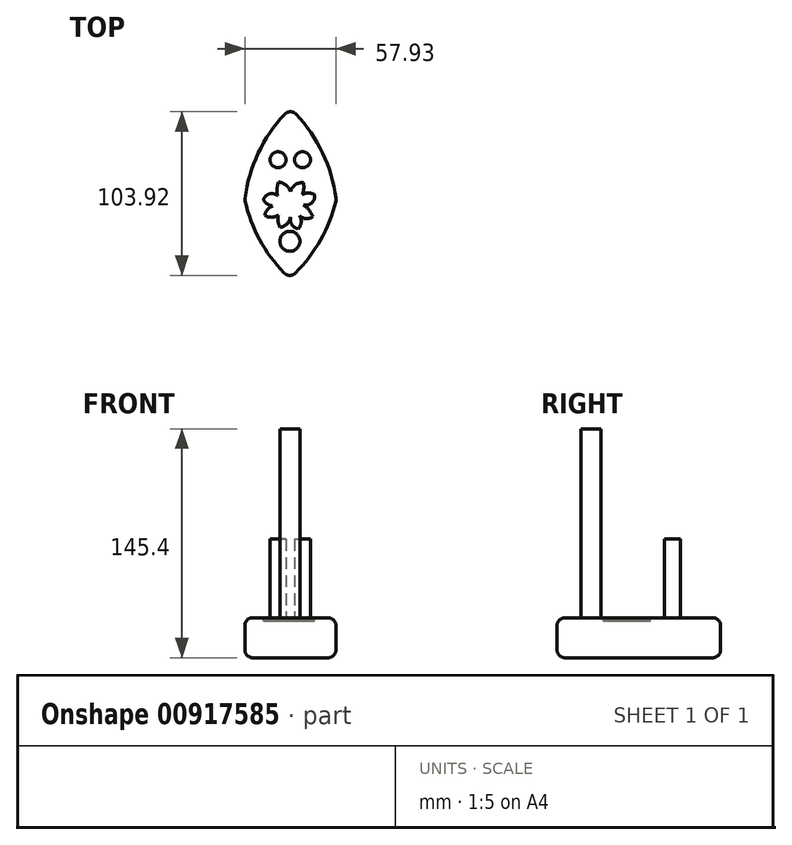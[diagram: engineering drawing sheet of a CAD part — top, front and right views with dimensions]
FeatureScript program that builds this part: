
annotation { "Feature Type Name" : "Feature", "Feature Type Description" : "" }
export const myFeature = defineFeature(function(context is Context, id is Id, definition is map)
    precondition{}
    {
        {
            var Q0;
            Q0=qCreatedBy(makeId("Top.planeOp"),FACE);
            var sketch = newSketch(context, id + "F0", { "sketchPlane" : qUnion([Q0])});
            skArc(sketch, "E0", {"start": v(0, 58.02) * mm, "mid": v(-19.52, 31.51) * mm, "end": v(-29.04, 0) * mm});
            skArc(sketch, "E1", {"start": v(-29.04, 0) * mm, "mid": v(-18.4, -27.48) * mm, "end": v(0, -50.5) * mm});
            skArc(sketch, "E2", {"start": v(-1.4, -50.82) * mm, "mid": v(17.8, -27.8) * mm, "end": v(29.04, 0) * mm});
            skArc(sketch, "E3", {"start": v(29.04, 0) * mm, "mid": v(19.52, 31.51) * mm, "end": v(0, 58.02) * mm});
            skSolve(sketch);
        }
        {
            var Q0;
            Q0 = qSketchRegion(id + "F0", true);
            extrude(context, id + "F1", {"entities" : qUnion([Q0]), "depth" : 25.4 * mm, "offsetDistance" : 25.4 * mm});
        }
        {
            var Q0;
            Q0=makeQuery(id+"F1.opExtrude","SWEPT_FACE",FACE,{"disambiguationData":[OSD([sQuery(id+"F0.wireOp",EDGE,"E1")])]});
            var Q1;
            Q1=makeQuery(id+"F1.opExtrude","SWEPT_FACE",FACE,{"disambiguationData":[OSD([sQuery(id+"F0.wireOp",EDGE,"E2")])]});
            var Q2;
            Q2=makeQuery(id+"F1.opExtrude","CAP_EDGE",EDGE,{"disambiguationData":[OSD([sQuery(id+"F0.wireOp",EDGE,"E3")])],"isStart":false});
            var Q3;
            Q3=makeQuery(id+"F1.opExtrude","CAP_EDGE",EDGE,{"disambiguationData":[OSD([sQuery(id+"F0.wireOp",EDGE,"E0")])],"isStart":false});
            var Q4;
            Q4=makeQuery(id+"F1.opExtrude","SWEPT_FACE",FACE,{"disambiguationData":[OSD([sQuery(id+"F0.wireOp",EDGE,"E0")])]});
            var Q5;
            Q5=makeQuery(id+"F1.opExtrude","SWEPT_FACE",FACE,{"disambiguationData":[OSD([sQuery(id+"F0.wireOp",EDGE,"E3")])]});
            var Q6;
            Q6=makeQuery(id+"F1.opExtrude","CAP_FACE",FACE,{"disambiguationData":[OSD([sQuery(id+"F0.wireOp",EDGE,"E0"),sQuery(id+"F0.wireOp",EDGE,"E1"),sQuery(id+"F0.wireOp",EDGE,"E2"),sQuery(id+"F0.wireOp",EDGE,"E3")])],"isStart":false});
            fillet(context, id + "F2", {"entities" : qUnion([Q0, Q1, Q2, Q3, Q4, Q5, Q6]), "radius" : 5.08 * mm, "tangentPropagation" : true, "allowEdgeOverflow" : false});
        }
        {
            var Q0;
            Q0=makeQuery(id+"F1.opExtrude","CAP_FACE",FACE,{"disambiguationData":[OSD([sQuery(id+"F0.wireOp",EDGE,"E0"),sQuery(id+"F0.wireOp",EDGE,"E1"),sQuery(id+"F0.wireOp",EDGE,"E2"),sQuery(id+"F0.wireOp",EDGE,"E3")])],"isStart":false});
            var sketch = newSketch(context, id + "F3", { "sketchPlane" : qUnion([Q0])});
            skLineSegment(sketch, "E4", {"start": v(-23.89, 0.24) * mm, "end": v(23.88, 0.27) * mm});
            skLineSegment(sketch, "E5", {"start": v(0, 50.79) * mm, "end": v(-0.45, -42.97) * mm});
            skCircle(sketch, "E6", {"center": v(-0.37, -26.4) * mm, "radius": 6.35 * mm});
            skCircle(sketch, "E7", {"center": v(-7.94, 25.39) * mm, "radius": 5.08 * mm});
            skCircle(sketch, "E8", {"center": v(7.7, 25.39) * mm, "radius": 5.08 * mm});
            skSolve(sketch);
        }
        {
            var Q0;
            {var subQ0=sQuery(id+"F3.wireOp",EDGE,"E6");var subQ1=sQuery(id+"F3.wireOp",EDGE,"E5");var subQ2=makeQuery(id+"F3.imprint","INTERSECT",VERTEX,{"disambiguationData":[OD(0.0)],"derivedFrom":[subQ1,subQ0]});Q0=makeQuery(id+"F3.imprint","IMPRINT",FACE,{"disambiguationData":[TD([[makeQuery(id+"F3.imprint","IMPRINT",EDGE,{"disambiguationData":[TD([[subQ2,-1.0]])],"derivedFrom":subQ1}),1.0]])]});}
            var Q1;
            {var subQ0=sQuery(id+"F3.wireOp",EDGE,"E6");var subQ1=sQuery(id+"F3.wireOp",EDGE,"E5");var subQ2=makeQuery(id+"F3.imprint","INTERSECT",VERTEX,{"disambiguationData":[OD(0.0)],"derivedFrom":[subQ1,subQ0]});Q1=makeQuery(id+"F3.imprint","IMPRINT",FACE,{"disambiguationData":[TD([[makeQuery(id+"F3.imprint","IMPRINT",EDGE,{"disambiguationData":[TD([[subQ2,-1.0]])],"derivedFrom":subQ1}),-1.0]])]});}
            extrude(context, id + "F4", {"entities" : qUnion([Q0, Q1]), "operationType" : NewBodyOperationType.ADD, "depth" : 120 * mm, "offsetDistance" : 25.4 * mm});
        }
        {
            var Q0;
            Q0=makeQuery(id+"F3.imprint","IMPRINT",FACE,{"disambiguationData":[TD([[makeQuery(id+"F3.imprint","IMPRINT",EDGE,{"derivedFrom":sQuery(id+"F3.wireOp",EDGE,"E8")}),1.0]])]});
            var Q1;
            Q1=makeQuery(id+"F3.imprint","IMPRINT",FACE,{"disambiguationData":[TD([[makeQuery(id+"F3.imprint","IMPRINT",EDGE,{"derivedFrom":sQuery(id+"F3.wireOp",EDGE,"E7")}),1.0]])]});
            var Q2;
            Q2=sQuery(id+"F3.wireOp",EDGE,"E7");
            var Q3;
            Q3=sQuery(id+"F3.wireOp",EDGE,"E8");
            extrude(context, id + "F5", {"entities" : qUnion([Q0, Q1]), "surfaceEntities" : qUnion([Q2, Q3]), "depth" : 50 * mm, "offsetDistance" : 25 * mm});
        }
        {
            var Q0;
            Q0=makeQuery(id+"F1.opExtrude","CAP_FACE",FACE,{"disambiguationData":[OSD([sQuery(id+"F0.wireOp",EDGE,"E0"),sQuery(id+"F0.wireOp",EDGE,"E1"),sQuery(id+"F0.wireOp",EDGE,"E2"),sQuery(id+"F0.wireOp",EDGE,"E3")])],"isStart":false});
            var sketch = newSketch(context, id + "F6", { "sketchPlane" : qUnion([Q0])});
            skArc(sketch, "E9", {"start": v(8.21, 10.77) * mm, "mid": v(3.08, 9.5) * mm, "end": v(0, 5.2) * mm});
            skArc(sketch, "E10", {"start": v(7.35, 3.2) * mm, "mid": v(8.43, 6.91) * mm, "end": v(8.21, 10.77) * mm});
            skArc(sketch, "E11", {"start": v(15.31, 3.2) * mm, "mid": v(11.33, 4.33) * mm, "end": v(7.35, 3.2) * mm});
            skArc(sketch, "E12", {"start": v(11.33, -3.27) * mm, "mid": v(14.52, -0.77) * mm, "end": v(15.31, 3.2) * mm});
            skArc(sketch, "E13", {"start": v(8.21, -3.27) * mm, "mid": v(9.77, -3.41) * mm, "end": v(11.33, -3.27) * mm});
            skArc(sketch, "E14", {"start": v(14.26, -10.69) * mm, "mid": v(11.81, -6.51) * mm, "end": v(8.21, -3.27) * mm});
            skArc(sketch, "E15", {"start": v(4.89, -8.84) * mm, "mid": v(9.16, -11.86) * mm, "end": v(14.26, -10.69) * mm});
            skArc(sketch, "E16", {"start": v(4.89, -18.55) * mm, "mid": v(6.89, -13.7) * mm, "end": v(4.89, -8.84) * mm});
            skArc(sketch, "E17", {"start": v(0, -13.7) * mm, "mid": v(1.7, -16.86) * mm, "end": v(4.89, -18.55) * mm});
            skArc(sketch, "E18", {"start": v(0, -13.7) * mm, "mid": v(0.06, -12.41) * mm, "end": v(0, -11.12) * mm});
            skArc(sketch, "E19", {"start": v(-6.62, -17.56) * mm, "mid": v(-2.25, -15.43) * mm, "end": v(0, -11.12) * mm});
            skArc(sketch, "E20", {"start": v(-7.7, -9.83) * mm, "mid": v(-7.93, -13.8) * mm, "end": v(-6.62, -17.56) * mm});
            skArc(sketch, "E21", {"start": v(0, 5.2) * mm, "mid": v(-2.92, 9.37) * mm, "end": v(-7.68, 11.18) * mm});
            skArc(sketch, "E22", {"start": v(-7.68, 11.18) * mm, "mid": v(-8.54, 6.9) * mm, "end": v(-8.24, 2.53) * mm});
            skArc(sketch, "E23", {"start": v(-8.24, 2.53) * mm, "mid": v(-13.37, 3.72) * mm, "end": v(-17.09, 0) * mm});
            skArc(sketch, "E24", {"start": v(-17.09, 0) * mm, "mid": v(-14.69, -2.65) * mm, "end": v(-11.39, -4.03) * mm});
            skArc(sketch, "E25", {"start": v(-11.39, -4.03) * mm, "mid": v(-14.63, -6.32) * mm, "end": v(-16.37, -9.89) * mm});
            skArc(sketch, "E26", {"start": v(-16.37, -9.89) * mm, "mid": v(-12.03, -11.17) * mm, "end": v(-7.7, -9.83) * mm});
            skSolve(sketch);
        }
        {
            var Q0;
            Q0 = qSketchRegion(id + "F6", true);
            extrude(context, id + "F7", {"entities" : qUnion([Q0]), "operationType" : NewBodyOperationType.REMOVE, "oppositeDirection" : true, "depth" : 2 * mm, "offsetDistance" : 25 * mm});
        }
    });
